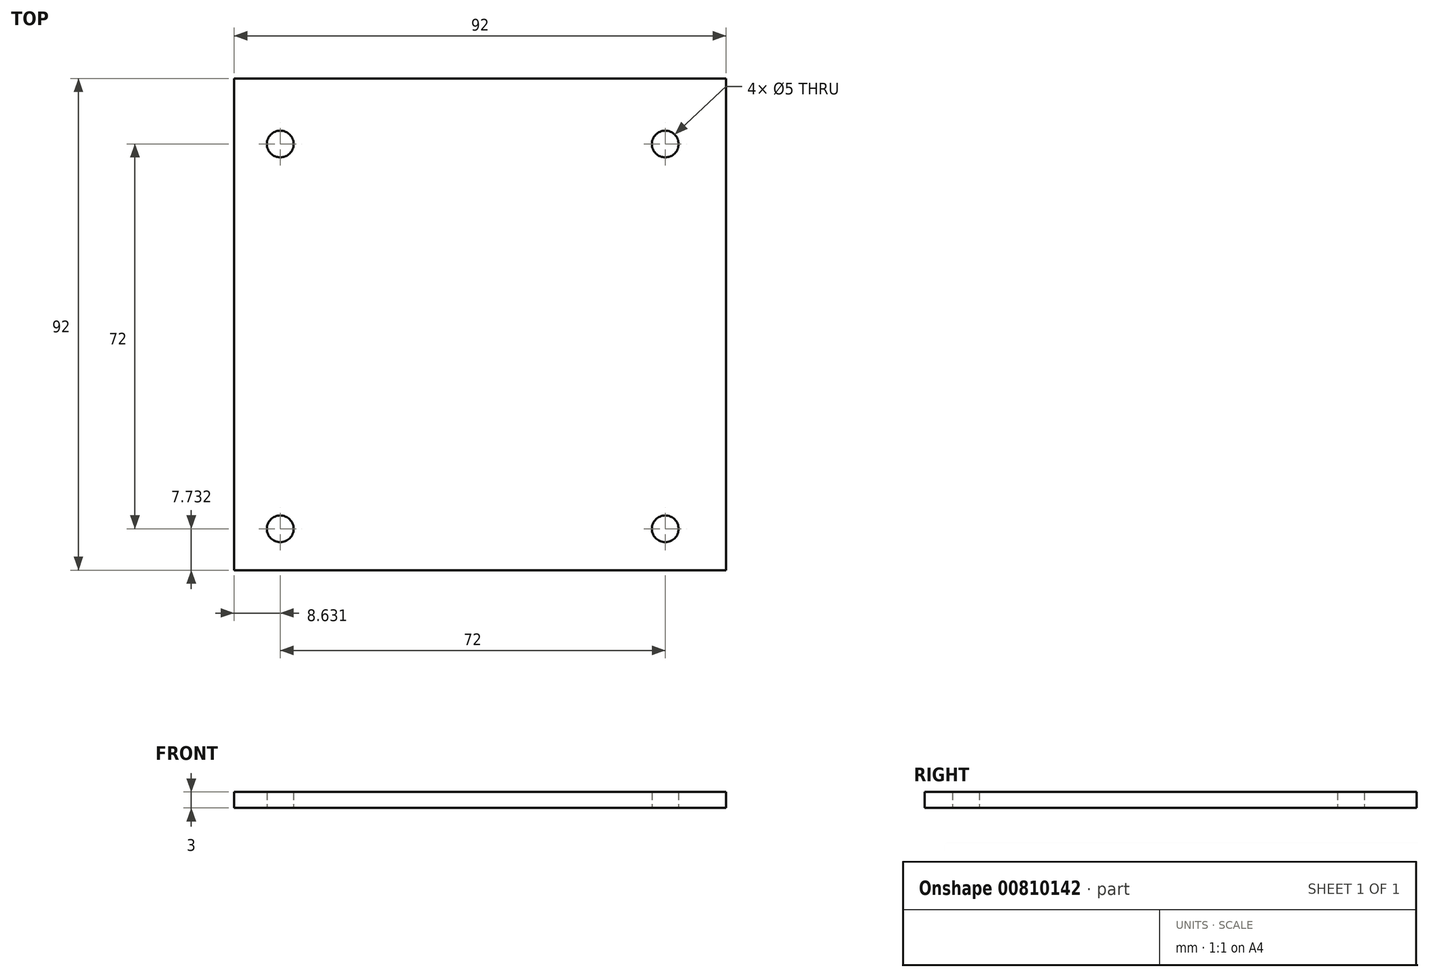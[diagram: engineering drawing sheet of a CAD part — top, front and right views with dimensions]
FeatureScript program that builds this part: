
annotation { "Feature Type Name" : "Feature", "Feature Type Description" : "" }
export const myFeature = defineFeature(function(context is Context, id is Id, definition is map)
    precondition{}
    {
        {
            var Q0;
            Q0=qCreatedBy(makeId("Top.planeOp"),FACE);
            var sketch = newSketch(context, id + "F0", { "sketchPlane" : qUnion([Q0])});
            skLineSegment(sketch, "E0.bottom", {"start": v(46, 46) * mm, "end": v(-46, 46) * mm});
            skLineSegment(sketch, "E0.top", {"start": v(46, -46) * mm, "end": v(-46, -46) * mm});
            skLineSegment(sketch, "E0.left", {"start": v(46, 46) * mm, "end": v(46, -46) * mm});
            skLineSegment(sketch, "E0.right", {"start": v(-46, 46) * mm, "end": v(-46, -46) * mm});
            skPoint(sketch, "E0.middle", {"position": v(0, 0) * mm});
            skCircle(sketch, "E1", {"center": v(-37.37, 33.73) * mm, "radius": 2.5 * mm});
            skCircle(sketch, "E2", {"center": v(34.63, 33.73) * mm, "radius": 2.5 * mm});
            skCircle(sketch, "E3", {"center": v(34.63, -38.27) * mm, "radius": 2.5 * mm});
            skCircle(sketch, "E4", {"center": v(-37.37, -38.27) * mm, "radius": 2.5 * mm});
            skSolve(sketch);
        }
        {
            var Q0;
            Q0=makeQuery(id+"F0.imprint","IMPRINT",FACE,{"disambiguationData":[TD([[makeQuery(id+"F0.imprint","IMPRINT",EDGE,{"derivedFrom":sQuery(id+"F0.wireOp",EDGE,"E0.bottom")}),1.0]])]});
            extrude(context, id + "F1", {"entities" : qUnion([Q0]), "depth" : 3 * mm, "offsetDistance" : 25 * mm});
        }
    });
